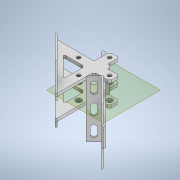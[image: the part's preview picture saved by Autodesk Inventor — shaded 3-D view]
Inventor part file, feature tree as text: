
AUTODESK INVENTOR PART (.ipt)
format: ipt  version: 2020 (Build 240168000, 168)  size: 536,576 bytes
history: native  units: mm
features: extrude x11, sketch x11, mirror x7, chamfer x6, plane x1
ambient origin geometry x8: Origin, YZ Plane, XZ Plane, XY Plane, X Axis, Y Axis, Z Axis, Center Point
bodies: Solid1 (feature_tree)
feature tree (36):
  extrude  "Extrusion1"  Depth=4.0mm
  chamfer  "Chamfer1"  Distance=5.0mm
  extrude  "Extrusion2"  Depth=5.0mm
  plane  "Work Plane1"
  mirror  "Mirror1"
  chamfer  "Chamfer2"  Distance=5.0mm
  extrude  "Extrusion3"  Depth=5.0mm
  chamfer  "Chamfer3"  Distance=3.0mm
  extrude  "Extrusion4"  Depth=2.0mm TaperAngle=45.0deg
  chamfer  "Chamfer4"  [1 undecoded]
  extrude  "Extrusion5"  Depth=3.0mm
  extrude  "Extrusion6"  Depth=25.0mm
  extrude  "Extrusion7"  Depth=1.5mm
  mirror  "Mirror5"
  mirror  "Mirror6"
  chamfer  "Chamfer5"  Distance=10.0mm
  extrude  "Extrusion8"  Depth=1.5mm TaperAngle=0.0deg
  chamfer  "Chamfer6"  Distance=5.0mm
  extrude  "Extrusion9"  Depth=5.0mm
  mirror  "Mirror7"
  mirror  "Mirror8"
  extrude  "Extrusion10"  Depth=3.0mm TaperAngle=0.0deg
  extrude  "Extrusion11"  Depth=3.0mm TaperAngle=45.0deg
  mirror  "Mirror9"
  mirror  "Mirror10"
  sketch  "Sketch1"  dims[d0=4.0mm d1=4.0mm]
  sketch  "Sketch3"  dims[d2=16.5mm]
  sketch  "Sketch4"  dims[d3=16.5mm]
  sketch  "Sketch5"  dims[d4=4.0mm]
  sketch  "Sketch6"  dims[d5=4.0mm]
  sketch  "Sketch7"  dims[d6=16.5mm]
  sketch  "Sketch8"  dims[d7=16.5mm]
  sketch  "Sketch9"  dims[d8=3.0mm]
  sketch  "Sketch10"  dims[d9=10.0mm]
  sketch  "Sketch11"  dims[d10=3.0mm]
  sketch  "Sketch12"  dims[d11=3.0mm d12=5.0mm d13=5.0mm d14=5.0mm d15=5.0mm d16=3.0mm d17=0.0mm d18=2.0mm d19=2.0mm d20=45.0deg d25=0.0mm d26=3.0mm d27=25.0mm d28=75.0mm d29=10.0mm d30=0.0mm d31=0.0mm d32=1.5mm d33=2.0mm d34=45.0deg d35=5.0mm d36=5.0mm d37=3.0mm d38=0.0mm d39=3.0mm d40=2.0mm d41=45.0deg d42=6.0mm d43=6.0mm d44=3.0mm d45=0.0mm d46=2.0mm d47=2.0mm d48=45.0deg d50=6.0mm d51=6.0mm d52=2.0mm d53=0.0mm d54=6.0mm d55=6.0mm d56=18.0mm d57=0.0mm d58=45.0deg d59=45.0deg d60=3.0mm d61=3.0mm d62=6.0mm d63=6.0mm d64=2.0mm d65=0.0mm d66=2.0mm d67=2.0mm d68=45.0deg d69=36.0mm d70=11.5mm d71=1.5mm d72=60.0mm d73=0.0mm d74=1.5mm d75=2.0mm d76=45.0deg d80=3.0mm d81=3.0mm d82=15.0mm d83=15.0mm d87=22.68928mm d88=3.0mm d89=6.0mm d90=10.0mm d91=6.0mm d92=0.0mm d93=0.0mm d94=18.0mm d95=3.0mm d96=0.0mm d97=3.0mm d98=3.0mm d101=22.274mm d102=22.274mm d103=1.414mm d104=0.0mm d105=0.0mm d106=3.0mm d107=3.0mm d108=2.75mm d109=0.0mm d110=9.0mm d112=4.5mm d113=1.5mm d114=0.0mm]
note: 1 required parameter value undecoded (feature->parameter linkage not recoverable at this tier; creation-order binding heuristic only, values carry confidence <= 0.55)
